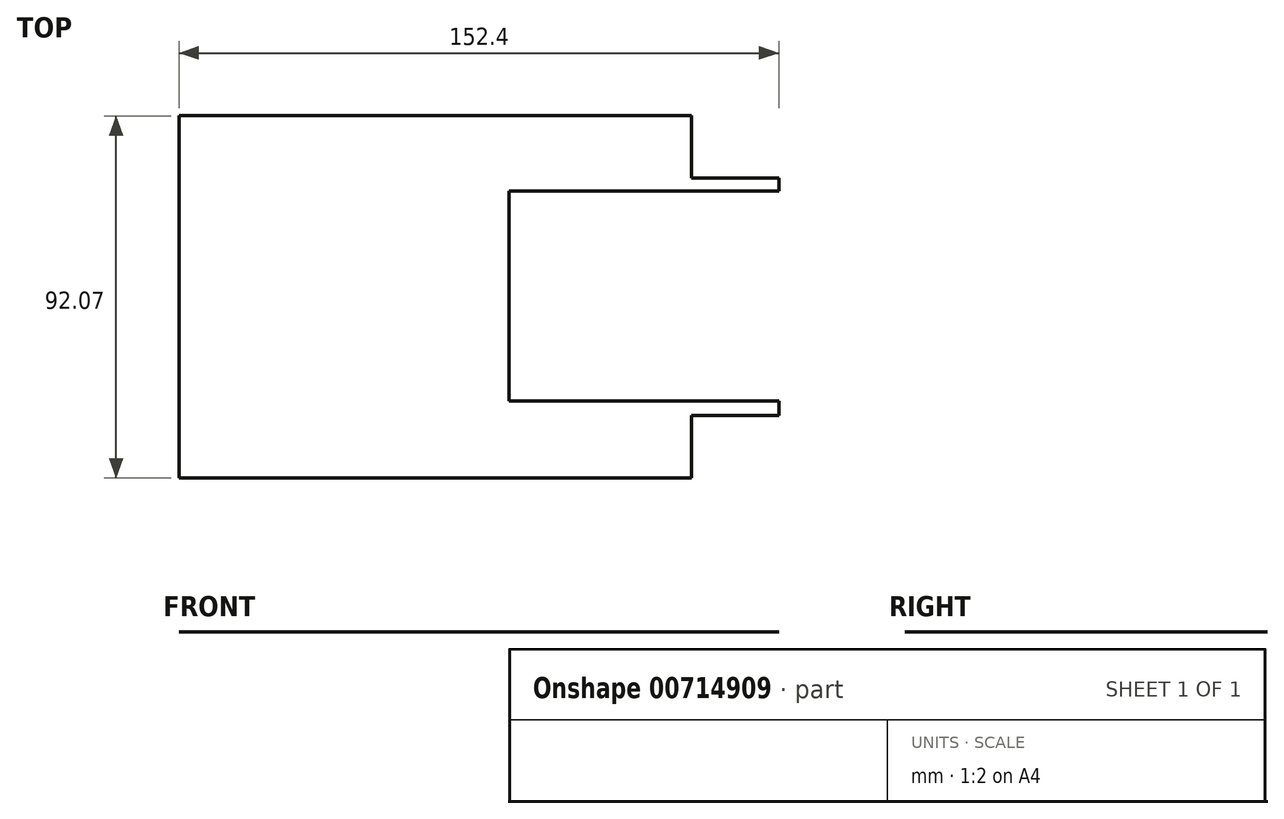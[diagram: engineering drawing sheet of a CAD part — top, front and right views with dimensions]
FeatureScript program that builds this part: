
annotation { "Feature Type Name" : "Feature", "Feature Type Description" : "" }
export const myFeature = defineFeature(function(context is Context, id is Id, definition is map)
    precondition{}
    {
        {
            var Q0;
            Q0=qCreatedBy(makeId("Top.planeOp"),FACE);
            var sketch = newSketch(context, id + "F0", { "sketchPlane" : qUnion([Q0])});
            skLineSegment(sketch, "E0.bottom", {"start": v(-172.53, 87.8) * mm, "end": v(-20.13, 87.8) * mm});
            skLineSegment(sketch, "E0.top", {"start": v(-172.53, -4.27) * mm, "end": v(-20.13, -4.27) * mm});
            skLineSegment(sketch, "E0.left", {"start": v(-172.53, 87.8) * mm, "end": v(-172.53, -4.27) * mm});
            skLineSegment(sketch, "E0.right", {"start": v(-20.13, 87.8) * mm, "end": v(-20.13, -4.27) * mm});
            skLineSegment(sketch, "E1.bottom", {"start": v(-20.13, -4.27) * mm, "end": v(-42.35, -4.27) * mm});
            skLineSegment(sketch, "E1.top", {"start": v(-20.13, 11.6) * mm, "end": v(-42.35, 11.6) * mm});
            skLineSegment(sketch, "E1.left", {"start": v(-20.13, -4.27) * mm, "end": v(-20.13, 11.6) * mm});
            skLineSegment(sketch, "E1.right", {"start": v(-42.35, -4.27) * mm, "end": v(-42.35, 11.6) * mm});
            skLineSegment(sketch, "E2.bottom", {"start": v(-20.13, 87.8) * mm, "end": v(-42.35, 87.8) * mm});
            skLineSegment(sketch, "E2.top", {"start": v(-20.13, 71.93) * mm, "end": v(-42.35, 71.93) * mm});
            skLineSegment(sketch, "E2.left", {"start": v(-20.13, 87.8) * mm, "end": v(-20.13, 71.93) * mm});
            skLineSegment(sketch, "E2.right", {"start": v(-42.35, 87.8) * mm, "end": v(-42.35, 71.93) * mm});
            skLineSegment(sketch, "E3.bottom", {"start": v(-20.13, 15.33) * mm, "end": v(-88.7, 15.33) * mm});
            skLineSegment(sketch, "E3.top", {"start": v(-20.13, 68.67) * mm, "end": v(-88.7, 68.67) * mm});
            skLineSegment(sketch, "E3.left", {"start": v(-20.13, 15.33) * mm, "end": v(-20.13, 68.67) * mm});
            skLineSegment(sketch, "E3.right", {"start": v(-88.7, 15.33) * mm, "end": v(-88.7, 68.67) * mm});
            skSolve(sketch);
        }
        {
            var Q0;
            {var subQ6=sQuery(id+"F0.wireOp",EDGE,"E0.left");Q0=makeQuery(id+"F0.imprint","IMPRINT",FACE,{"disambiguationData":[TD([[makeQuery(id+"F0.imprint","IMPRINT",EDGE,{"derivedFrom":subQ6}),1.0]])]});}
            extrude(context, id + "F1", {"entities" : qUnion([Q0]), "oppositeDirection" : true, "depth" : 1 / 203.2 * mm, "offsetDistance" : 25.4 * mm});
        }
    });
